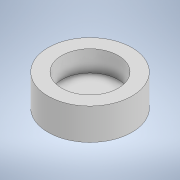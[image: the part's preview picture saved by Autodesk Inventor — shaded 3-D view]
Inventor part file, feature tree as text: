
AUTODESK INVENTOR PART (.ipt)
format: ipt  version: 2020 (Build 240168000, 168)  size: 154,112 bytes
history: native  units: in
note: dims shown in document units (in); Inventor stores cm internally (conversion verified against a paired STEP export)
features: sketch x6, extrude x3, revolve x2, thread x1, helix x1
ambient origin geometry x8: Origin, YZ Plane, XZ Plane, XY Plane, X Axis, Y Axis, Z Axis, Center Point
bodies: Solid1 (feature_tree), Solid2 (feature_tree)
feature tree (13):
  extrude  "Extrusion1"  Depth=0.375in TaperAngle=0.0deg
  extrude  "Extrusion2"  Depth=0.25in TaperAngle=0.0deg
  extrude  "Extrusion3"  Depth=0.25in TaperAngle=0.0deg
  revolve  "Revolution2"  [1 undecoded]
  thread  "Thread1"  [1 undecoded]
  revolve  "Revolution1"  [1 undecoded]
  helix  "Coil1"  [1 undecoded]
  sketch  "Sketch1"  dims[d0=1.0in d1=0.375in d2=0.0in]
  sketch  "Sketch2"  dims[d3=0.675in d4=0.25in d5=0.0in]
  sketch  "Sketch3"  dims[d6=0.25in d7=0.25in d8=0.0in]
  sketch  "Sketch4"  dims[d9=0.5in d10=0.0in d11=0.3779in d12=0.008in d13=0.008in d16=0.05in]
  sketch  "Sketch5"  dims[d18=0.3779in d20=0.0in d21=0.0in]
  sketch  "Sketch6"  dims[d22=0.05in d23=0.6in d24=0.3937in d25=0.0in d26=0.0in d27=0.0in d28=0.0in d29=0.0in]
note: 4 required parameter values undecoded (feature->parameter linkage not recoverable at this tier; creation-order binding heuristic only, values carry confidence <= 0.55)